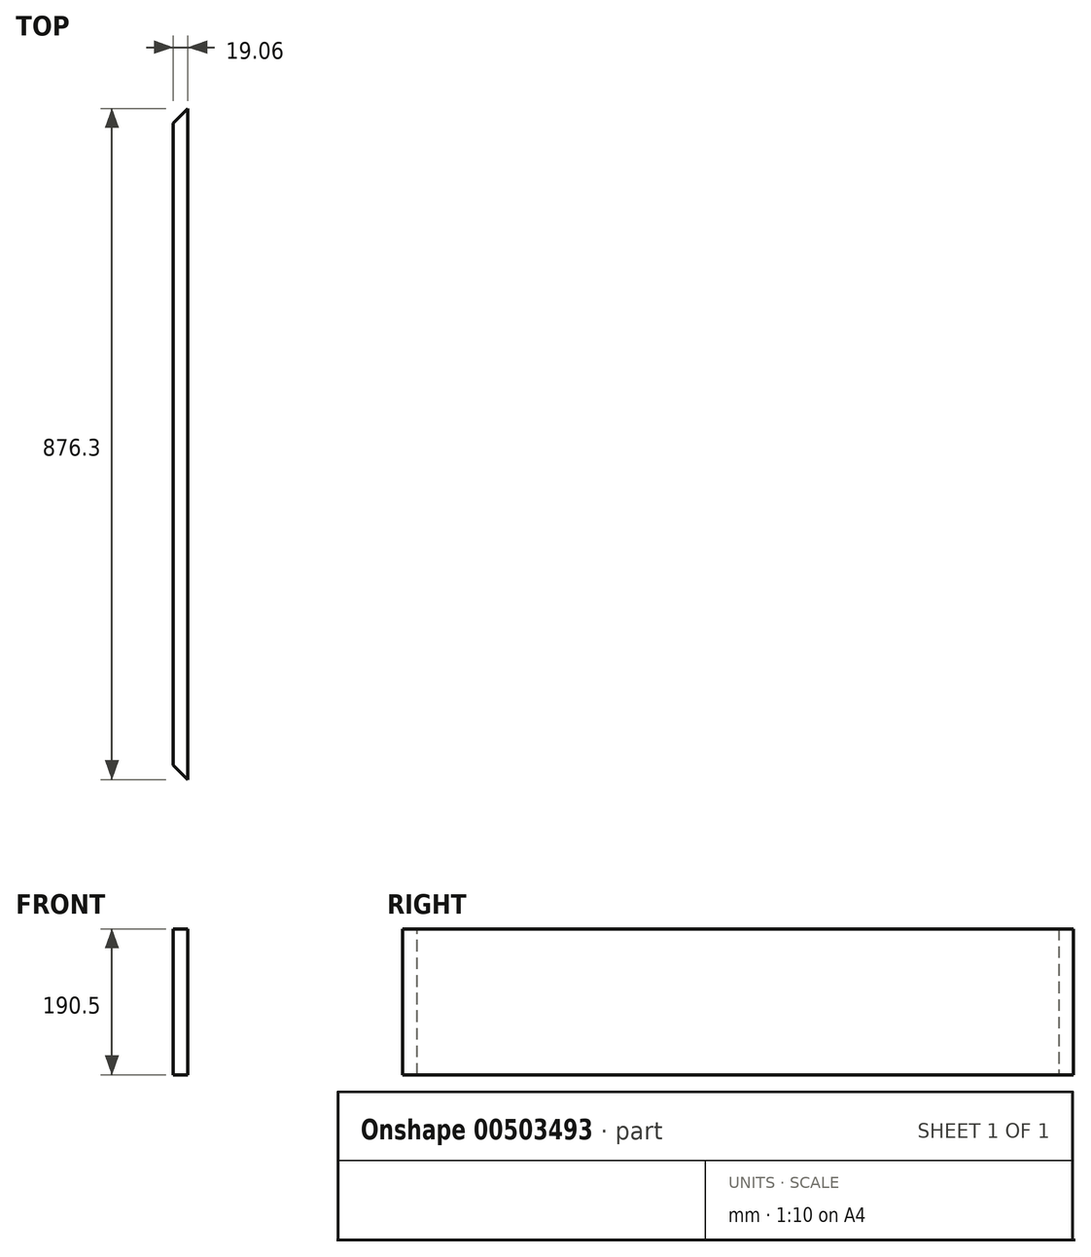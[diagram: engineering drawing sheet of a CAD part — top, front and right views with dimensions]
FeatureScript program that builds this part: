
annotation { "Feature Type Name" : "Feature", "Feature Type Description" : "" }
export const myFeature = defineFeature(function(context is Context, id is Id, definition is map)
    precondition{}
    {
        {
            var Q0;
            Q0=qCreatedBy(makeId("Front.planeOp"),FACE);
            var sketch = newSketch(context, id + "F0", { "sketchPlane" : qUnion([Q0])});
            skLineSegment(sketch, "E0", {"start": v(0, 68.9) * mm, "end": v(0, -40.32) * mm, "construction": true});
            skLineSegment(sketch, "E1", {"start": v(-64.45, 0) * mm, "end": v(67.63, 0) * mm, "construction": true});
            skLineSegment(sketch, "E2.bottom", {"start": v(-9.53, -95.25) * mm, "end": v(9.52, -95.25) * mm});
            skLineSegment(sketch, "E2.top", {"start": v(-9.53, 95.25) * mm, "end": v(9.52, 95.25) * mm});
            skLineSegment(sketch, "E2.left", {"start": v(-9.53, -95.25) * mm, "end": v(-9.53, 95.25) * mm});
            skLineSegment(sketch, "E2.right", {"start": v(9.53, -95.25) * mm, "end": v(9.53, 95.25) * mm});
            skSolve(sketch);
        }
        {
            var Q0;
            Q0 = qSketchRegion(id + "F0", true);
            extrude(context, id + "F1", {"entities" : qUnion([Q0]), "endBound" : BoundingType.SYMMETRIC, "depth" : 914.4 * mm});
        }
        {
            var Q0;
            Q0=makeQuery(id+"F1.opExtrude","CAP_EDGE",EDGE,{"disambiguationData":[OSD([sQuery(id+"F0.wireOp",EDGE,"E2.left")])],"isStart":true});
            var Q1;
            Q1=makeQuery(id+"F1.opExtrude","CAP_EDGE",EDGE,{"disambiguationData":[OSD([sQuery(id+"F0.wireOp",EDGE,"E2.left")])],"isStart":false});
            chamfer(context, id + "F2", {"entities" : qUnion([Q0, Q1]), "width" : 38.1 * mm, "tangentPropagation" : true});
        }
    });
